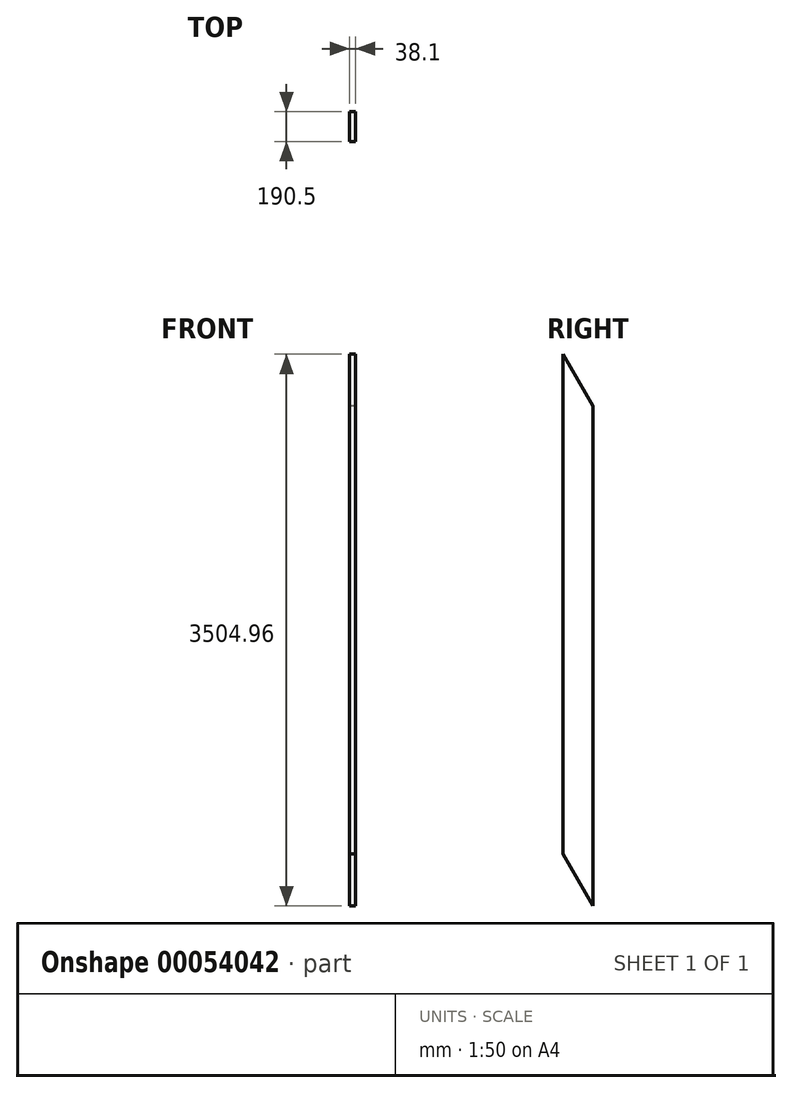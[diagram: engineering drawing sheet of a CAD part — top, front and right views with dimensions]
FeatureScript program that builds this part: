
annotation { "Feature Type Name" : "Feature", "Feature Type Description" : "" }
export const myFeature = defineFeature(function(context is Context, id is Id, definition is map)
    precondition{}
    {
        {
            var Q0;
            Q0=qCreatedBy(makeId("Right.planeOp"),FACE);
            var sketch = newSketch(context, id + "F0", { "sketchPlane" : qUnion([Q0])});
            skLineSegment(sketch, "E0", {"start": v(0, 0) * mm, "end": v(-190.5, 329.96) * mm});
            skLineSegment(sketch, "E1", {"start": v(-190.5, 329.96) * mm, "end": v(-190.5, 3504.96) * mm});
            skLineSegment(sketch, "E2", {"start": v(-190.5, 3504.96) * mm, "end": v(0, 3175) * mm});
            skLineSegment(sketch, "E3", {"start": v(0, 3175) * mm, "end": v(0, 0) * mm});
            skSolve(sketch);
        }
        {
            var Q0;
            Q0=makeQuery(id+"F0.imprint","IMPRINT",FACE,{"disambiguationData":[TD([[makeQuery(id+"F0.imprint","IMPRINT",EDGE,{"derivedFrom":sQuery(id+"F0.wireOp",EDGE,"E0")}),-1.0]])]});
            extrude(context, id + "F1", {"entities" : qUnion([Q0]), "depth" : 38.1 * mm});
        }
    });
